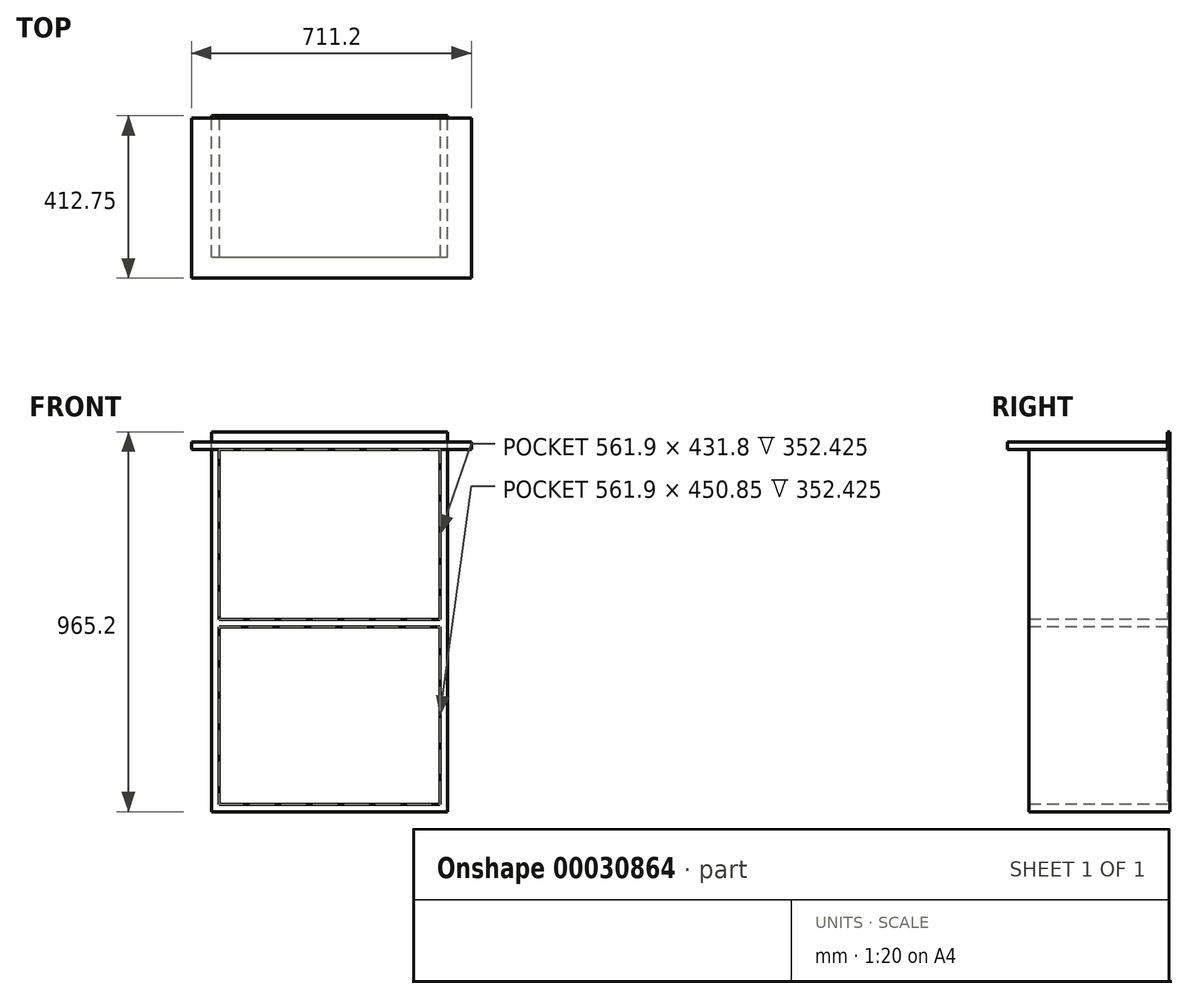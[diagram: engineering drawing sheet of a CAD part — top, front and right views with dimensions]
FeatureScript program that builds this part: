
annotation { "Feature Type Name" : "Feature", "Feature Type Description" : "" }
export const myFeature = defineFeature(function(context is Context, id is Id, definition is map)
    precondition{}
    {
        {
            var Q0;
            Q0=qCreatedBy(makeId("Front.planeOp"),FACE);
            var sketch = newSketch(context, id + "F0", { "sketchPlane" : qUnion([Q0])});
            skLineSegment(sketch, "E0.bottom", {"start": v(-300, 469.9) * mm, "end": v(300, 469.9) * mm});
            skLineSegment(sketch, "E0.top", {"start": v(-300, -469.9) * mm, "end": v(300, -469.9) * mm});
            skLineSegment(sketch, "E0.left", {"start": v(-300, 469.9) * mm, "end": v(-300, -469.9) * mm});
            skLineSegment(sketch, "E0.right", {"start": v(300, 469.9) * mm, "end": v(300, -469.9) * mm});
            skLineSegment(sketch, "E1", {"start": v(300, 469.9) * mm, "end": v(-300, -469.9) * mm, "construction": true});
            skSolve(sketch);
        }
        {
            var Q0;
            Q0 = qSketchRegion(id + "F0", true);
            extrude(context, id + "F1", {"entities" : qUnion([Q0]), "endBound" : BoundingType.SYMMETRIC, "depth" : 355.6 * mm});
        }
        {
            var Q0;
            Q0=makeQuery(id+"F1.opExtrude","CAP_FACE",FACE,{"disambiguationData":[OSD([sQuery(id+"F0.wireOp",EDGE,"E0.bottom"),sQuery(id+"F0.wireOp",EDGE,"E0.top"),sQuery(id+"F0.wireOp",EDGE,"E0.left"),sQuery(id+"F0.wireOp",EDGE,"E0.right")])],"isStart":false});
            var sketch = newSketch(context, id + "F2", { "sketchPlane" : qUnion([Q0])});
            skLineSegment(sketch, "E2.bottom", {"start": v(-280.95, 450.85) * mm, "end": v(280.95, 450.85) * mm});
            skLineSegment(sketch, "E2.top", {"start": v(-280.95, 19.05) * mm, "end": v(280.95, 19.05) * mm});
            skLineSegment(sketch, "E2.left", {"start": v(-280.95, 450.85) * mm, "end": v(-280.95, 19.05) * mm});
            skLineSegment(sketch, "E2.right", {"start": v(280.95, 450.85) * mm, "end": v(280.95, 19.05) * mm});
            skLineSegment(sketch, "E3.bottom", {"start": v(-280.95, 0) * mm, "end": v(280.95, 0) * mm});
            skLineSegment(sketch, "E3.top", {"start": v(-280.95, -450.85) * mm, "end": v(280.95, -450.85) * mm});
            skLineSegment(sketch, "E3.left", {"start": v(-280.95, 0) * mm, "end": v(-280.95, -450.85) * mm});
            skLineSegment(sketch, "E3.right", {"start": v(280.95, 0) * mm, "end": v(280.95, -450.85) * mm});
            skLineSegment(sketch, "E4.0", {"start": v(-280.95, 450.85) * mm, "end": v(280.95, 450.85) * mm, "construction": true});
            skLineSegment(sketch, "E4.1", {"start": v(-280.95, 450.85) * mm, "end": v(-280.95, -450.85) * mm, "construction": true});
            skLineSegment(sketch, "E4.2", {"start": v(-280.95, -450.85) * mm, "end": v(280.95, -450.85) * mm, "construction": true});
            skLineSegment(sketch, "E4.3", {"start": v(280.95, 450.85) * mm, "end": v(280.95, -450.85) * mm, "construction": true});
            skSolve(sketch);
        }
        {
            var Q0;
            Q0 = qSketchRegion(id + "F2", true);
            extrude(context, id + "F3", {"entities" : qUnion([Q0]), "operationType" : NewBodyOperationType.REMOVE, "endBound" : BoundingType.THROUGH_ALL, "oppositeDirection" : true, "depth" : 25.4 * mm});
        }
        {
            var Q0;
            Q0=makeQuery(id+"F1.opExtrude","CAP_FACE",FACE,{"disambiguationData":[OSD([sQuery(id+"F0.wireOp",EDGE,"E0.bottom"),sQuery(id+"F0.wireOp",EDGE,"E0.top"),sQuery(id+"F0.wireOp",EDGE,"E0.left"),sQuery(id+"F0.wireOp",EDGE,"E0.right")])],"isStart":true});
            var sketch = newSketch(context, id + "F4", { "sketchPlane" : qUnion([Q0])});
            skLineSegment(sketch, "E5.1", {"start": v(300, -469.9) * mm, "end": v(-300, -469.9) * mm});
            skLineSegment(sketch, "E5.2", {"start": v(300, 495.3) * mm, "end": v(300, -469.9) * mm});
            skLineSegment(sketch, "E6.2", {"start": v(-300, 495.3) * mm, "end": v(-300, -469.9) * mm});
            skLineSegment(sketch, "E7", {"start": v(-300, 495.3) * mm, "end": v(300, 495.3) * mm});
            skSolve(sketch);
        }
        {
            var Q0;
            Q0 = qSketchRegion(id + "F4", true);
            var Q1;
            Q1=sQuery(id+"F4.wireOp",EDGE,"E7");
            extrude(context, id + "F5", {"entities" : qUnion([Q0]), "operationType" : NewBodyOperationType.ADD, "surfaceEntities" : qUnion([Q1]), "endBound" : BoundingType.SYMMETRIC, "depth" : 6.35 * mm});
        }
        {
            var Q0;
            Q0=makeQuery(id+"F1.opExtrude","SWEPT_FACE",FACE,{"disambiguationData":[OSD([sQuery(id+"F0.wireOp",EDGE,"E0.bottom")])]});
            var sketch = newSketch(context, id + "F6", { "sketchPlane" : qUnion([Q0])});
            skLineSegment(sketch, "E8.bottom", {"start": v(-350.8, -231.77) * mm, "end": v(360.4, -231.77) * mm});
            skLineSegment(sketch, "E8.top", {"start": v(-350.8, 174.62) * mm, "end": v(360.4, 174.62) * mm});
            skLineSegment(sketch, "E8.left", {"start": v(-350.8, -231.77) * mm, "end": v(-350.8, 174.62) * mm});
            skLineSegment(sketch, "E8.right", {"start": v(360.4, -231.77) * mm, "end": v(360.4, 174.62) * mm});
            skSolve(sketch);
        }
        {
            var Q0;
            Q0=makeQuery(id+"F6.imprint","IMPRINT",FACE,{"disambiguationData":[TD([[makeQuery(id+"F6.imprint","IMPRINT",EDGE,{"derivedFrom":sQuery(id+"F6.wireOp",EDGE,"E8.bottom")}),1.0]])]});
            extrude(context, id + "F7", {"entities" : qUnion([Q0]), "operationType" : NewBodyOperationType.ADD, "oppositeDirection" : true, "depth" : 19.05 * mm});
        }
    });
